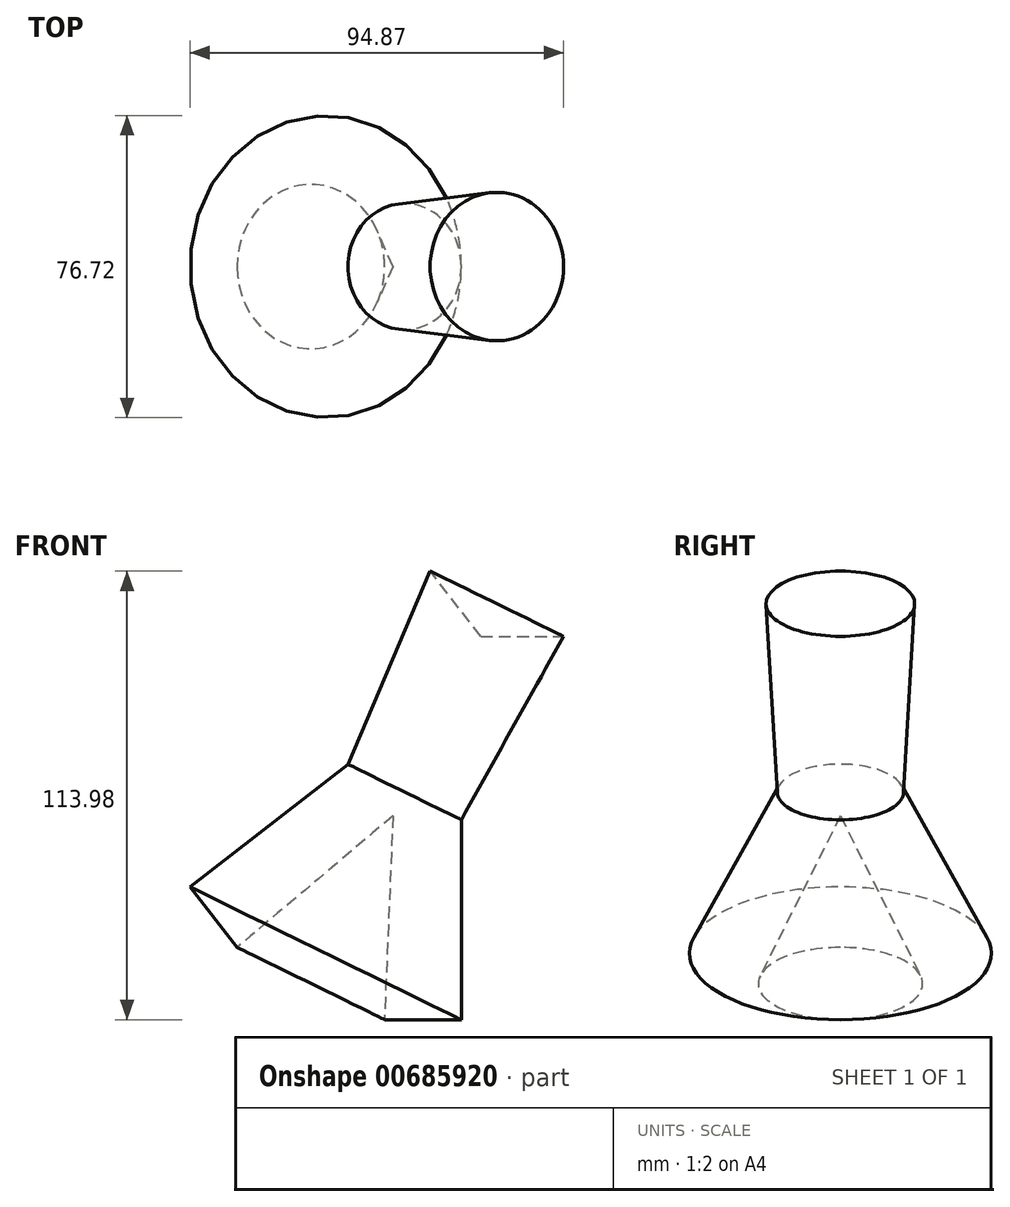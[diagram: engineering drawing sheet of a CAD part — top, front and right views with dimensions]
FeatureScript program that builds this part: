
annotation { "Feature Type Name" : "Feature", "Feature Type Description" : "" }
export const myFeature = defineFeature(function(context is Context, id is Id, definition is map)
    precondition{}
    {
        {
            var Q0;
            Q0=qCreatedBy(makeId("Front.planeOp"),FACE);
            var sketch = newSketch(context, id + "F0", { "sketchPlane" : qUnion([Q0])});
            skLineSegment(sketch, "E0", {"start": v(-11.55, -42.3) * mm, "end": v(7.92, -42.3) * mm});
            skLineSegment(sketch, "E1", {"start": v(7.92, -42.3) * mm, "end": v(7.92, 8.5) * mm});
            skLineSegment(sketch, "E2", {"start": v(7.92, 8.5) * mm, "end": v(33.9, 55.1) * mm});
            skLineSegment(sketch, "E3", {"start": v(33.9, 55.1) * mm, "end": v(12.89, 55.1) * mm});
            skLineSegment(sketch, "E4", {"start": v(12.89, 55.1) * mm, "end": v(-9.45, 9.45) * mm});
            skLineSegment(sketch, "E5", {"start": v(-9.45, 9.45) * mm, "end": v(-11.55, -42.3) * mm});
            skSolve(sketch);
        }
        {
            var Q0;
            Q0 = qSketchRegion(id + "F0", true);
            var Q1;
            Q1=sQuery(id+"F0.wireOp",EDGE,"E4");
            revolve(context, id + "F1", {"surfaceOperationType" : NewSurfaceOperationType.NEW, "entities" : qUnion([Q0]), "axis" : qUnion([Q1]), "revolveType" : RevolveType.FULL});
        }
    });
